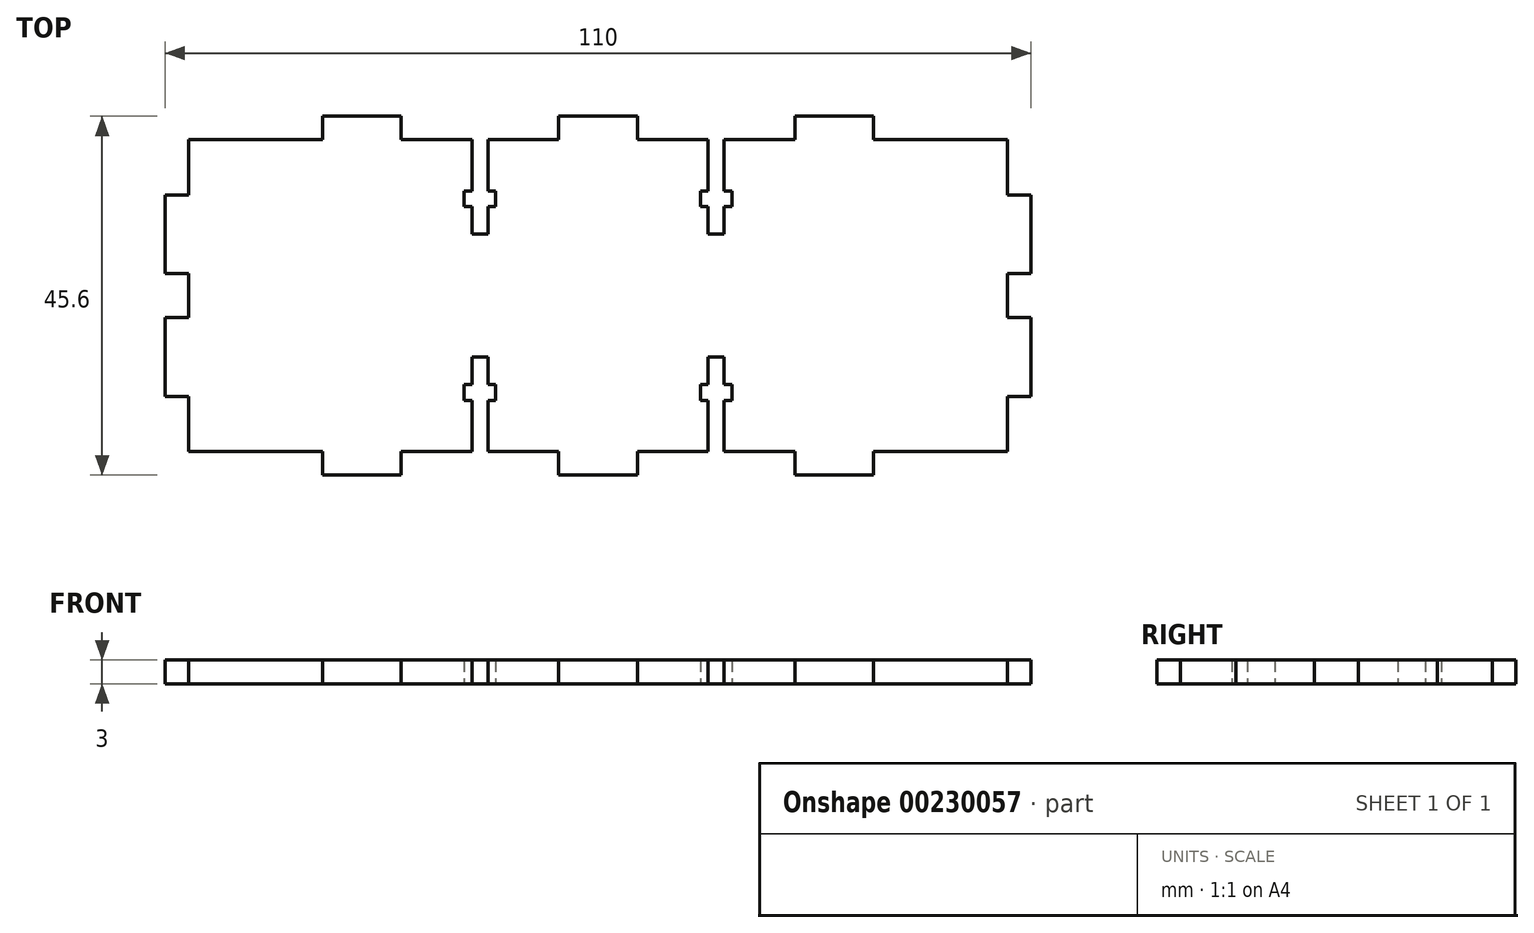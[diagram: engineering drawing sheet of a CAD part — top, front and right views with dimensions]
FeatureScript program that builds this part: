
annotation { "Feature Type Name" : "Feature", "Feature Type Description" : "" }
export const myFeature = defineFeature(function(context is Context, id is Id, definition is map)
    precondition{}
    {
        {
            var Q0;
            Q0=qCreatedBy(makeId("Top.planeOp"),FACE);
            var sketch = newSketch(context, id + "F0", { "sketchPlane" : qUnion([Q0])});
            skLineSegment(sketch, "E0", {"start": v(0, 0) * mm, "end": v(17, 0) * mm});
            skLineSegment(sketch, "E1", {"start": v(17, 0) * mm, "end": v(17, -3) * mm});
            skLineSegment(sketch, "E2", {"start": v(17, -3) * mm, "end": v(27, -3) * mm});
            skLineSegment(sketch, "E3", {"start": v(27, -3) * mm, "end": v(27, 0) * mm});
            skLineSegment(sketch, "E4", {"start": v(47, 0) * mm, "end": v(47, -3) * mm});
            skLineSegment(sketch, "E5", {"start": v(47, -3) * mm, "end": v(57, -3) * mm});
            skLineSegment(sketch, "E6", {"start": v(57, -3) * mm, "end": v(57, 0) * mm});
            skLineSegment(sketch, "E7", {"start": v(77, 0) * mm, "end": v(77, -3) * mm});
            skLineSegment(sketch, "E8", {"start": v(77, -3) * mm, "end": v(87, -3) * mm});
            skLineSegment(sketch, "E9", {"start": v(87, -3) * mm, "end": v(87, 0) * mm});
            skLineSegment(sketch, "E10", {"start": v(87, 0) * mm, "end": v(104, 0) * mm});
            skLineSegment(sketch, "E11", {"start": v(104, 0) * mm, "end": v(104, 7) * mm});
            skLineSegment(sketch, "E12", {"start": v(104, 7) * mm, "end": v(107, 7) * mm});
            skLineSegment(sketch, "E13", {"start": v(107, 7) * mm, "end": v(107, 17) * mm});
            skLineSegment(sketch, "E14", {"start": v(107, 17) * mm, "end": v(104, 17) * mm});
            skLineSegment(sketch, "E15", {"start": v(104, 17) * mm, "end": v(104, 22.6) * mm});
            skLineSegment(sketch, "E16", {"start": v(104, 22.6) * mm, "end": v(107, 22.6) * mm});
            skLineSegment(sketch, "E17", {"start": v(107, 22.6) * mm, "end": v(107, 32.6) * mm});
            skLineSegment(sketch, "E18", {"start": v(107, 32.6) * mm, "end": v(104, 32.6) * mm});
            skLineSegment(sketch, "E19", {"start": v(104, 32.6) * mm, "end": v(104, 39.6) * mm});
            skLineSegment(sketch, "E20", {"start": v(104, 39.6) * mm, "end": v(87, 39.6) * mm});
            skLineSegment(sketch, "E21", {"start": v(87, 39.6) * mm, "end": v(87, 42.6) * mm});
            skLineSegment(sketch, "E22", {"start": v(87, 42.6) * mm, "end": v(77, 42.6) * mm});
            skLineSegment(sketch, "E23", {"start": v(77, 42.6) * mm, "end": v(77, 39.6) * mm});
            skLineSegment(sketch, "E24", {"start": v(57, 39.6) * mm, "end": v(57, 42.6) * mm});
            skLineSegment(sketch, "E25", {"start": v(57, 42.6) * mm, "end": v(47, 42.6) * mm});
            skLineSegment(sketch, "E26", {"start": v(47, 42.6) * mm, "end": v(47, 39.6) * mm});
            skLineSegment(sketch, "E27", {"start": v(27, 39.6) * mm, "end": v(27, 42.6) * mm});
            skLineSegment(sketch, "E28", {"start": v(27, 42.6) * mm, "end": v(17, 42.6) * mm});
            skLineSegment(sketch, "E29", {"start": v(17, 42.6) * mm, "end": v(17, 39.6) * mm});
            skLineSegment(sketch, "E30", {"start": v(17, 39.6) * mm, "end": v(0, 39.6) * mm});
            skLineSegment(sketch, "E31", {"start": v(0, 39.6) * mm, "end": v(0, 32.6) * mm});
            skLineSegment(sketch, "E32", {"start": v(0, 32.6) * mm, "end": v(-3, 32.6) * mm});
            skLineSegment(sketch, "E33", {"start": v(-3, 32.6) * mm, "end": v(-3, 22.6) * mm});
            skLineSegment(sketch, "E34", {"start": v(-3, 22.6) * mm, "end": v(0, 22.6) * mm});
            skLineSegment(sketch, "E35", {"start": v(0, 22.6) * mm, "end": v(0, 17) * mm});
            skLineSegment(sketch, "E36", {"start": v(0, 17) * mm, "end": v(-3, 17) * mm});
            skLineSegment(sketch, "E37", {"start": v(-3, 17) * mm, "end": v(-3, 7) * mm});
            skLineSegment(sketch, "E38", {"start": v(-3, 7) * mm, "end": v(0, 7) * mm});
            skLineSegment(sketch, "E39", {"start": v(0, 7) * mm, "end": v(0, 0) * mm});
            skLineSegment(sketch, "E40.top", {"start": v(36, 12) * mm, "end": v(38, 12) * mm});
            skLineSegment(sketch, "E41.left", {"start": v(35, 8.5) * mm, "end": v(35, 6.5) * mm});
            skLineSegment(sketch, "E41.right", {"start": v(39, 8.5) * mm, "end": v(39, 6.5) * mm});
            skLineSegment(sketch, "E42", {"start": v(35, 8.5) * mm, "end": v(36, 8.5) * mm});
            skLineSegment(sketch, "E43", {"start": v(35, 6.5) * mm, "end": v(36, 6.5) * mm});
            skLineSegment(sketch, "E44", {"start": v(39, 6.5) * mm, "end": v(38, 6.5) * mm});
            skLineSegment(sketch, "E45", {"start": v(39, 8.5) * mm, "end": v(38, 8.5) * mm});
            skLineSegment(sketch, "E46", {"start": v(36, 6.5) * mm, "end": v(36, 0) * mm});
            skLineSegment(sketch, "E47", {"start": v(36, 12) * mm, "end": v(36, 8.5) * mm});
            skLineSegment(sketch, "E48", {"start": v(38, 12) * mm, "end": v(38, 8.5) * mm});
            skLineSegment(sketch, "E49", {"start": v(38, 6.5) * mm, "end": v(38, 0) * mm});
            skLineSegment(sketch, "E50", {"start": v(27, 0) * mm, "end": v(36, 0) * mm});
            skLineSegment(sketch, "E51", {"start": v(38, 0) * mm, "end": v(47, 0) * mm});
            skLineSegment(sketch, "E52.MirrorCS", {"start": v(36, 27.6) * mm, "end": v(38, 27.6) * mm});
            skLineSegment(sketch, "E53.MirrorCS", {"start": v(35, 31.1) * mm, "end": v(35, 33.1) * mm});
            skLineSegment(sketch, "E54.MirrorCS", {"start": v(35, 31.1) * mm, "end": v(36, 31.1) * mm});
            skLineSegment(sketch, "E55.MirrorCS", {"start": v(39, 31.1) * mm, "end": v(38, 31.1) * mm});
            skLineSegment(sketch, "E56.MirrorCS", {"start": v(35, 33.1) * mm, "end": v(36, 33.1) * mm});
            skLineSegment(sketch, "E57.MirrorCS", {"start": v(39, 33.1) * mm, "end": v(38, 33.1) * mm});
            skLineSegment(sketch, "E58.MirrorCS", {"start": v(39, 31.1) * mm, "end": v(39, 33.1) * mm});
            skLineSegment(sketch, "E59.MirrorCS", {"start": v(36, 27.6) * mm, "end": v(36, 31.1) * mm});
            skLineSegment(sketch, "E60.MirrorCS", {"start": v(36, 33.1) * mm, "end": v(36, 39.6) * mm});
            skLineSegment(sketch, "E61.MirrorCS", {"start": v(38, 27.6) * mm, "end": v(38, 31.1) * mm});
            skLineSegment(sketch, "E62.MirrorCS", {"start": v(38, 33.1) * mm, "end": v(38, 39.6) * mm});
            skLineSegment(sketch, "E63", {"start": v(27, 39.6) * mm, "end": v(36, 39.6) * mm});
            skLineSegment(sketch, "E64", {"start": v(38, 39.6) * mm, "end": v(47, 39.6) * mm});
            skLineSegment(sketch, "E65.MirrorCS", {"start": v(68, 12) * mm, "end": v(66, 12) * mm});
            skLineSegment(sketch, "E66.MirrorCS", {"start": v(68, 27.6) * mm, "end": v(66, 27.6) * mm});
            skLineSegment(sketch, "E67.MirrorCS", {"start": v(69, 8.5) * mm, "end": v(68, 8.5) * mm});
            skLineSegment(sketch, "E68.MirrorCS", {"start": v(69, 31.1) * mm, "end": v(69, 33.1) * mm});
            skLineSegment(sketch, "E69.MirrorCS", {"start": v(65, 6.5) * mm, "end": v(66, 6.5) * mm});
            skLineSegment(sketch, "E70.MirrorCS", {"start": v(69, 6.5) * mm, "end": v(68, 6.5) * mm});
            skLineSegment(sketch, "E71.MirrorCS", {"start": v(65, 31.1) * mm, "end": v(65, 33.1) * mm});
            skLineSegment(sketch, "E72.MirrorCS", {"start": v(69, 33.1) * mm, "end": v(68, 33.1) * mm});
            skLineSegment(sketch, "E73.MirrorCS", {"start": v(69, 8.5) * mm, "end": v(69, 6.5) * mm});
            skLineSegment(sketch, "E74.MirrorCS", {"start": v(69, 31.1) * mm, "end": v(68, 31.1) * mm});
            skLineSegment(sketch, "E75.MirrorCS", {"start": v(65, 8.5) * mm, "end": v(65, 6.5) * mm});
            skLineSegment(sketch, "E76.MirrorCS", {"start": v(65, 33.1) * mm, "end": v(66, 33.1) * mm});
            skLineSegment(sketch, "E77.MirrorCS", {"start": v(65, 8.5) * mm, "end": v(66, 8.5) * mm});
            skLineSegment(sketch, "E78.MirrorCS", {"start": v(65, 31.1) * mm, "end": v(66, 31.1) * mm});
            skLineSegment(sketch, "E79.MirrorCS", {"start": v(66, 12) * mm, "end": v(66, 8.5) * mm});
            skLineSegment(sketch, "E80.MirrorCS", {"start": v(66, 27.6) * mm, "end": v(66, 31.1) * mm});
            skLineSegment(sketch, "E81.MirrorCS", {"start": v(66, 33.1) * mm, "end": v(66, 39.6) * mm});
            skLineSegment(sketch, "E82.MirrorCS", {"start": v(68, 12) * mm, "end": v(68, 8.5) * mm});
            skLineSegment(sketch, "E83.MirrorCS", {"start": v(66, 6.5) * mm, "end": v(66, 0) * mm});
            skLineSegment(sketch, "E84.MirrorCS", {"start": v(68, 6.5) * mm, "end": v(68, 0) * mm});
            skLineSegment(sketch, "E85.MirrorCS", {"start": v(68, 33.1) * mm, "end": v(68, 39.6) * mm});
            skLineSegment(sketch, "E86.MirrorCS", {"start": v(68, 27.6) * mm, "end": v(68, 31.1) * mm});
            skLineSegment(sketch, "E87", {"start": v(57, 0) * mm, "end": v(66, 0) * mm});
            skLineSegment(sketch, "E88", {"start": v(68, 0) * mm, "end": v(77, 0) * mm});
            skLineSegment(sketch, "E89", {"start": v(57, 39.6) * mm, "end": v(66, 39.6) * mm});
            skLineSegment(sketch, "E90", {"start": v(68, 39.6) * mm, "end": v(77, 39.6) * mm});
            skSolve(sketch);
        }
        {
            var Q0;
            Q0 = qSketchRegion(id + "F0", true);
            extrude(context, id + "F1", {"entities" : qUnion([Q0]), "depth" : 3 * mm});
        }
    });
